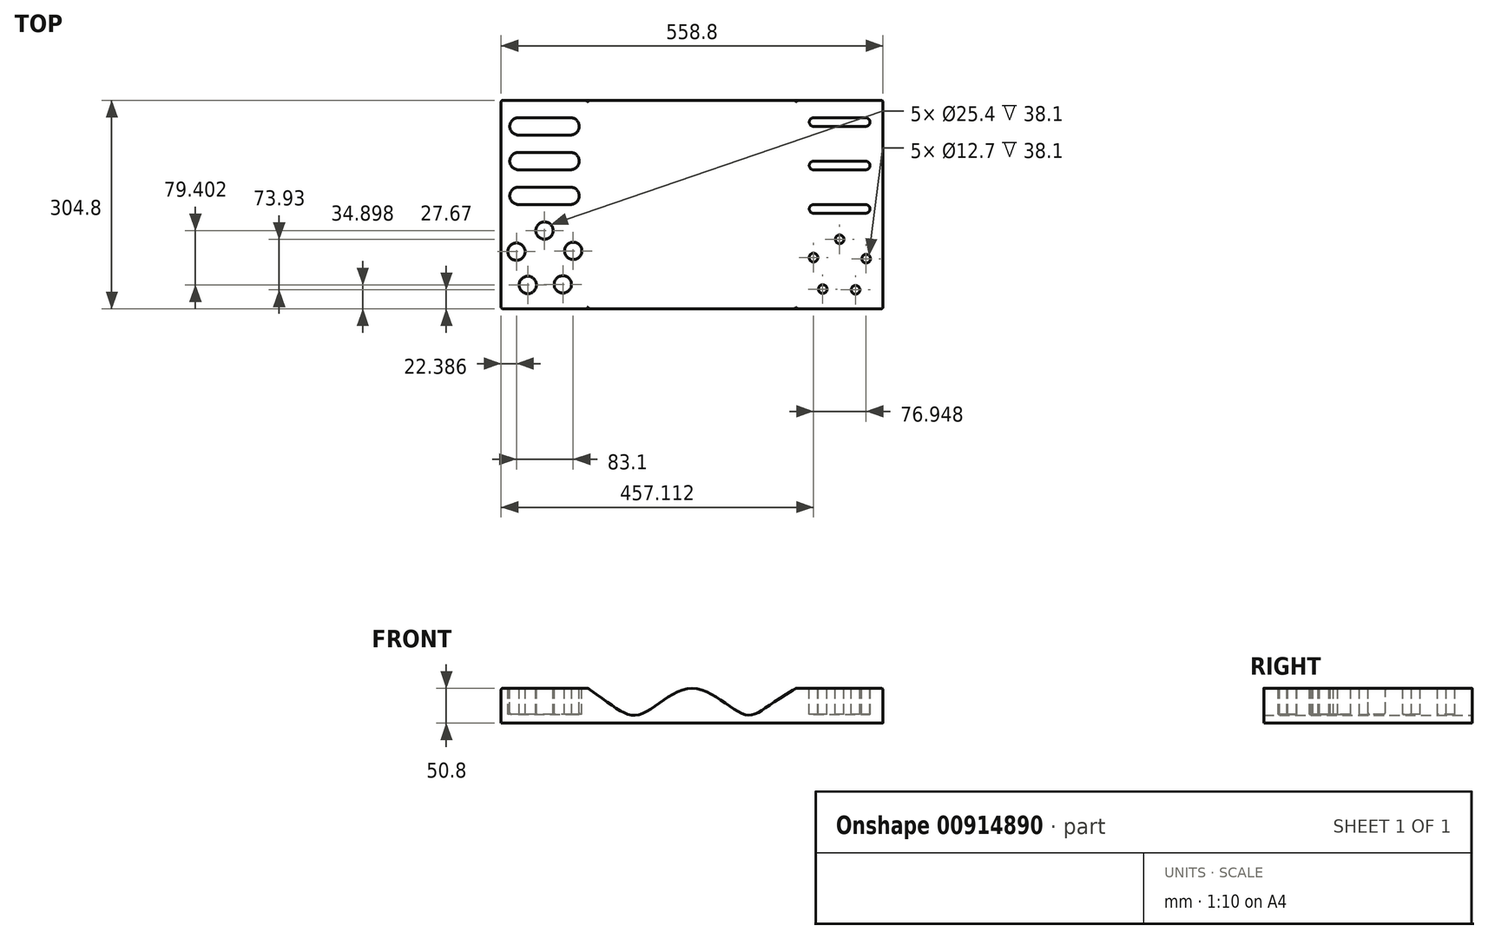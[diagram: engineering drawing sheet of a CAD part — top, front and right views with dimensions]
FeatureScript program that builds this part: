
annotation { "Feature Type Name" : "Feature", "Feature Type Description" : "" }
export const myFeature = defineFeature(function(context is Context, id is Id, definition is map)
    precondition{}
    {
        {
            var Q0;
            Q0=qCreatedBy(makeId("Front.planeOp"),FACE);
            var sketch = newSketch(context, id + "F0", { "sketchPlane" : qUnion([Q0])});
            skLineSegment(sketch, "E0.bottom", {"start": v(-259.7, 38.1) * mm, "end": v(-132.7, 38.1) * mm});
            skLineSegment(sketch, "E0.top", {"start": v(-259.7, -12.7) * mm, "end": v(299.1, -12.7) * mm});
            skLineSegment(sketch, "E0.left", {"start": v(-259.7, 38.1) * mm, "end": v(-259.7, -12.7) * mm});
            skLineSegment(sketch, "E0.right", {"start": v(299.1, 38.1) * mm, "end": v(299.1, -12.7) * mm});
            skPoint(sketch, "E1", {"position": v(172.1, 38.1) * mm});
            skPoint(sketch, "E2", {"position": v(19.7, 38.1) * mm});
            skPoint(sketch, "E3", {"position": v(-132.7, 38.1) * mm});
            skFitSpline(sketch, "E4", {"points": [v(172.1, 38.1) * mm, v(95.9, 0) * mm, v(19.7, 38.1) * mm, v(-56.5, 0) * mm, v(-132.7, 38.1) * mm], "startDerivative": vector(-541.44, -296.38) * mm, "endDerivative": vector(-454.84, 309.23) * mm});
            skLineSegment(sketch, "E5.trimOffspring", {"start": v(19.5, 38.1) * mm, "end": v(19.7, 38.1) * mm});
            skLineSegment(sketch, "E6.trimOffspring", {"start": v(172.1, 38.1) * mm, "end": v(299.1, 38.1) * mm});
            skSolve(sketch);
        }
        {
            var Q0;
            Q0=makeQuery(id+"F0.imprint","IMPRINT",FACE,{"disambiguationData":[TD([[makeQuery(id+"F0.imprint","IMPRINT",EDGE,{"derivedFrom":sQuery(id+"F0.wireOp",EDGE,"E0.bottom")}),-1.0]])]});
            extrude(context, id + "F1", {"entities" : qUnion([Q0]), "depth" : 304.8 * mm, "offsetDistance" : 25.4 * mm});
        }
        {
            var Q0;
            Q0=makeQuery(id+"F1.opExtrude","SWEPT_FACE",FACE,{"disambiguationData":[OSD([sQuery(id+"F0.wireOp",EDGE,"E0.bottom")])]});
            var sketch = newSketch(context, id + "F2", { "sketchPlane" : qUnion([Q0])});
            skLineSegment(sketch, "E7.bottom", {"start": v(-234.3, -25.4) * mm, "end": v(-158.1, -25.4) * mm});
            skLineSegment(sketch, "E7.top", {"start": v(-234.3, -50.8) * mm, "end": v(-158.1, -50.8) * mm});
            skArc(sketch, "E8", {"start": v(-234.3, -25.4) * mm, "mid": v(-247, -38.1) * mm, "end": v(-234.3, -50.8) * mm});
            skArc(sketch, "E9", {"start": v(-158.1, -50.8) * mm, "mid": v(-145.4, -38.1) * mm, "end": v(-158.1, -25.4) * mm});
            skArc(sketch, "E10.0.1.0", {"start": v(-234.3, -76.2) * mm, "mid": v(-247, -88.9) * mm, "end": v(-234.3, -101.6) * mm});
            skLineSegment(sketch, "E10.0.1.1", {"start": v(-234.3, -101.6) * mm, "end": v(-158.1, -101.6) * mm});
            skLineSegment(sketch, "E10.0.1.2", {"start": v(-234.3, -76.2) * mm, "end": v(-158.1, -76.2) * mm});
            skArc(sketch, "E10.0.1.3", {"start": v(-158.1, -101.6) * mm, "mid": v(-145.4, -88.9) * mm, "end": v(-158.1, -76.2) * mm});
            skArc(sketch, "E10.0.2.0", {"start": v(-234.3, -127) * mm, "mid": v(-247, -139.7) * mm, "end": v(-234.3, -152.4) * mm});
            skLineSegment(sketch, "E10.0.2.1", {"start": v(-234.3, -152.4) * mm, "end": v(-158.1, -152.4) * mm});
            skLineSegment(sketch, "E10.0.2.2", {"start": v(-234.3, -127) * mm, "end": v(-158.1, -127) * mm});
            skArc(sketch, "E10.0.2.3", {"start": v(-158.1, -152.4) * mm, "mid": v(-145.4, -139.7) * mm, "end": v(-158.1, -127) * mm});
            skLineSegment(sketch, "E10.direction1", {"start": v(-234.3, -50.8) * mm, "end": v(-208.9, -50.8) * mm, "construction": true});
            skLineSegment(sketch, "E10.direction2", {"start": v(-234.3, -50.8) * mm, "end": v(-234.3, -101.6) * mm, "construction": true});
            skCircle(sketch, "E11", {"center": v(-196.2, -190.5) * mm, "radius": 12.7 * mm});
            skCircle(sketch, "E12.1.0", {"center": v(-237.32, -221.29) * mm, "radius": 12.7 * mm});
            skCircle(sketch, "E12.2.0", {"center": v(-220.75, -269.9) * mm, "radius": 12.7 * mm});
            skCircle(sketch, "E12.3.0", {"center": v(-169.4, -269.16) * mm, "radius": 12.7 * mm});
            skCircle(sketch, "E12.4.0", {"center": v(-154.22, -220.09) * mm, "radius": 12.7 * mm});
            skPoint(sketch, "E12.center", {"position": v(-195.58, -234.19) * mm});
            skSolve(sketch);
        }
        {
            var Q0;
            Q0=makeQuery(id+"F2.imprint","IMPRINT",FACE,{"disambiguationData":[TD([[makeQuery(id+"F2.imprint","IMPRINT",EDGE,{"derivedFrom":sQuery(id+"F2.wireOp",EDGE,"E7.bottom")}),-1.0]])]});
            var Q1;
            Q1=makeQuery(id+"F2.imprint","IMPRINT",FACE,{"disambiguationData":[TD([[makeQuery(id+"F2.imprint","IMPRINT",EDGE,{"derivedFrom":sQuery(id+"F2.wireOp",EDGE,"E10.0.1.0")}),1.0]])]});
            var Q2;
            Q2=makeQuery(id+"F2.imprint","IMPRINT",FACE,{"disambiguationData":[TD([[makeQuery(id+"F2.imprint","IMPRINT",EDGE,{"derivedFrom":sQuery(id+"F2.wireOp",EDGE,"E10.0.2.0")}),1.0]])]});
            var Q3;
            Q3=makeQuery(id+"F2.imprint","IMPRINT",FACE,{"disambiguationData":[TD([[makeQuery(id+"F2.imprint","IMPRINT",EDGE,{"derivedFrom":sQuery(id+"F2.wireOp",EDGE,"E11")}),1.0]])]});
            var Q4;
            Q4=makeQuery(id+"F2.imprint","IMPRINT",FACE,{"disambiguationData":[TD([[makeQuery(id+"F2.imprint","IMPRINT",EDGE,{"derivedFrom":sQuery(id+"F2.wireOp",EDGE,"E12.4.0")}),1.0]])]});
            var Q5;
            Q5=makeQuery(id+"F2.imprint","IMPRINT",FACE,{"disambiguationData":[TD([[makeQuery(id+"F2.imprint","IMPRINT",EDGE,{"derivedFrom":sQuery(id+"F2.wireOp",EDGE,"E12.3.0")}),1.0]])]});
            var Q6;
            Q6=makeQuery(id+"F2.imprint","IMPRINT",FACE,{"disambiguationData":[TD([[makeQuery(id+"F2.imprint","IMPRINT",EDGE,{"derivedFrom":sQuery(id+"F2.wireOp",EDGE,"E12.2.0")}),1.0]])]});
            var Q7;
            Q7=makeQuery(id+"F2.imprint","IMPRINT",FACE,{"disambiguationData":[TD([[makeQuery(id+"F2.imprint","IMPRINT",EDGE,{"derivedFrom":sQuery(id+"F2.wireOp",EDGE,"E12.1.0")}),1.0]])]});
            extrude(context, id + "F3", {"entities" : qUnion([Q0, Q1, Q2, Q3, Q4, Q5, Q6, Q7]), "operationType" : NewBodyOperationType.REMOVE, "oppositeDirection" : true, "depth" : 38.1 * mm, "offsetDistance" : 25.4 * mm});
        }
        {
            var Q0;
            Q0=makeQuery(id+"F1.opExtrude","SWEPT_FACE",FACE,{"disambiguationData":[OSD([sQuery(id+"F0.wireOp",EDGE,"E6.trimOffspring")])]});
            var sketch = newSketch(context, id + "F4", { "sketchPlane" : qUnion([Q0])});
            skLineSegment(sketch, "E13.bottom", {"start": v(197.5, -25.4) * mm, "end": v(273.7, -25.4) * mm});
            skLineSegment(sketch, "E13.top", {"start": v(197.5, -38.1) * mm, "end": v(273.7, -38.1) * mm});
            skArc(sketch, "E14", {"start": v(273.7, -38.1) * mm, "mid": v(280.04, -31.75) * mm, "end": v(273.7, -25.4) * mm});
            skArc(sketch, "E15", {"start": v(197.5, -38.1) * mm, "mid": v(191.14, -31.75) * mm, "end": v(197.5, -25.4) * mm});
            skArc(sketch, "E16.0.1.0", {"start": v(273.7, -101.6) * mm, "mid": v(280.04, -95.25) * mm, "end": v(273.7, -88.9) * mm});
            skLineSegment(sketch, "E16.0.1.1", {"start": v(197.5, -101.6) * mm, "end": v(273.7, -101.6) * mm});
            skLineSegment(sketch, "E16.0.1.2", {"start": v(197.5, -88.9) * mm, "end": v(273.7, -88.9) * mm});
            skArc(sketch, "E16.0.1.3", {"start": v(197.5, -101.6) * mm, "mid": v(191.14, -95.25) * mm, "end": v(197.5, -88.9) * mm});
            skArc(sketch, "E16.0.2.0", {"start": v(273.7, -165.1) * mm, "mid": v(280.04, -158.75) * mm, "end": v(273.7, -152.4) * mm});
            skLineSegment(sketch, "E16.0.2.1", {"start": v(197.5, -165.1) * mm, "end": v(273.7, -165.1) * mm});
            skLineSegment(sketch, "E16.0.2.2", {"start": v(197.5, -152.4) * mm, "end": v(273.7, -152.4) * mm});
            skArc(sketch, "E16.0.2.3", {"start": v(197.5, -165.1) * mm, "mid": v(191.14, -158.75) * mm, "end": v(197.5, -152.4) * mm});
            skLineSegment(sketch, "E16.direction1", {"start": v(197.5, -38.1) * mm, "end": v(222.9, -38.1) * mm, "construction": true});
            skLineSegment(sketch, "E16.direction2", {"start": v(197.5, -38.1) * mm, "end": v(197.5, -101.6) * mm, "construction": true});
            skCircle(sketch, "E17", {"center": v(235.6, -203.2) * mm, "radius": 6.35 * mm});
            skCircle(sketch, "E18.1.0", {"center": v(274.35, -231.62) * mm, "radius": 6.35 * mm});
            skCircle(sketch, "E18.2.0", {"center": v(258.9, -277.13) * mm, "radius": 6.35 * mm});
            skCircle(sketch, "E18.3.0", {"center": v(210.85, -276.08) * mm, "radius": 6.35 * mm});
            skCircle(sketch, "E18.4.0", {"center": v(197.4, -229.94) * mm, "radius": 6.35 * mm});
            skPoint(sketch, "E18.center", {"position": v(235.6, -243.84) * mm});
            skLineSegment(sketch, "E18.anchor1", {"start": v(235.6, -243.84) * mm, "end": v(235.6, -203.2) * mm, "construction": true});
            skLineSegment(sketch, "E18.anchor2", {"start": v(235.6, -243.84) * mm, "end": v(197.4, -229.94) * mm, "construction": true});
            skSolve(sketch);
        }
        {
            var Q0;
            Q0=makeQuery(id+"F4.imprint","IMPRINT",FACE,{"disambiguationData":[TD([[makeQuery(id+"F4.imprint","IMPRINT",EDGE,{"derivedFrom":sQuery(id+"F4.wireOp",EDGE,"E13.bottom")}),-1.0]])]});
            var Q1;
            Q1=makeQuery(id+"F4.imprint","IMPRINT",FACE,{"disambiguationData":[TD([[makeQuery(id+"F4.imprint","IMPRINT",EDGE,{"derivedFrom":sQuery(id+"F4.wireOp",EDGE,"E16.0.1.0")}),1.0]])]});
            var Q2;
            Q2=makeQuery(id+"F4.imprint","IMPRINT",FACE,{"disambiguationData":[TD([[makeQuery(id+"F4.imprint","IMPRINT",EDGE,{"derivedFrom":sQuery(id+"F4.wireOp",EDGE,"E16.0.2.0")}),1.0]])]});
            var Q3;
            Q3=makeQuery(id+"F4.imprint","IMPRINT",FACE,{"disambiguationData":[TD([[makeQuery(id+"F4.imprint","IMPRINT",EDGE,{"derivedFrom":sQuery(id+"F4.wireOp",EDGE,"E17")}),1.0]])]});
            var Q4;
            Q4=makeQuery(id+"F4.imprint","IMPRINT",FACE,{"disambiguationData":[TD([[makeQuery(id+"F4.imprint","IMPRINT",EDGE,{"derivedFrom":sQuery(id+"F4.wireOp",EDGE,"E18.1.0")}),1.0]])]});
            var Q5;
            Q5=makeQuery(id+"F4.imprint","IMPRINT",FACE,{"disambiguationData":[TD([[makeQuery(id+"F4.imprint","IMPRINT",EDGE,{"derivedFrom":sQuery(id+"F4.wireOp",EDGE,"E18.2.0")}),1.0]])]});
            var Q6;
            Q6=makeQuery(id+"F4.imprint","IMPRINT",FACE,{"disambiguationData":[TD([[makeQuery(id+"F4.imprint","IMPRINT",EDGE,{"derivedFrom":sQuery(id+"F4.wireOp",EDGE,"E18.3.0")}),1.0]])]});
            var Q7;
            Q7=makeQuery(id+"F4.imprint","IMPRINT",FACE,{"disambiguationData":[TD([[makeQuery(id+"F4.imprint","IMPRINT",EDGE,{"derivedFrom":sQuery(id+"F4.wireOp",EDGE,"E18.4.0")}),1.0]])]});
            extrude(context, id + "F5", {"entities" : qUnion([Q0, Q1, Q2, Q3, Q4, Q5, Q6, Q7]), "operationType" : NewBodyOperationType.REMOVE, "oppositeDirection" : true, "depth" : 38.1 * mm, "offsetDistance" : 25.4 * mm});
        }
        {
            var Q0;
            Q0=makeQuery(id+"F1.opExtrude","SWEPT_EDGE",EDGE,{"disambiguationData":[OSD([sQuery(id+"F0.wireOp",EDGE,"E0.bottom"),sQuery(id+"F0.wireOp",EDGE,"E4")])]});
            var Q1;
            Q1=makeQuery(id+"F1.opExtrude","CAP_EDGE",EDGE,{"disambiguationData":[OSD([sQuery(id+"F0.wireOp",EDGE,"E0.bottom")])],"isStart":false});
            var Q2;
            Q2=makeQuery(id+"F1.opExtrude","SWEPT_EDGE",EDGE,{"disambiguationData":[OSD([sQuery(id+"F0.wireOp",EDGE,"E0.bottom"),sQuery(id+"F0.wireOp",EDGE,"E0.left")])]});
            var Q3;
            Q3=makeQuery(id+"F1.opExtrude","CAP_EDGE",EDGE,{"disambiguationData":[OSD([sQuery(id+"F0.wireOp",EDGE,"E0.bottom")])],"isStart":true});
            var Q4;
            Q4=makeQuery(id+"F3.boolean.opBoolean","COPY",EDGE,{"derivedFrom":makeQuery(id+"F3.opExtrude","CAP_EDGE",EDGE,{"disambiguationData":[OSD([sQuery(id+"F2.wireOp",EDGE,"E7.bottom")])],"isStart":true})});
            var Q5;
            Q5=makeQuery(id+"F3.boolean.opBoolean","COPY",EDGE,{"derivedFrom":makeQuery(id+"F3.opExtrude","CAP_EDGE",EDGE,{"disambiguationData":[OSD([sQuery(id+"F2.wireOp",EDGE,"E8")])],"isStart":true})});
            var Q6;
            Q6=makeQuery(id+"F3.boolean.opBoolean","COPY",EDGE,{"derivedFrom":makeQuery(id+"F3.opExtrude","CAP_EDGE",EDGE,{"disambiguationData":[OSD([sQuery(id+"F2.wireOp",EDGE,"E10.0.1.3")])],"isStart":true})});
            var Q7;
            Q7=makeQuery(id+"F3.boolean.opBoolean","COPY",FACE,{"derivedFrom":makeQuery(id+"F3.opExtrude","SWEPT_FACE",FACE,{"disambiguationData":[OSD([sQuery(id+"F2.wireOp",EDGE,"E10.0.2.3")])]})});
            var Q8;
            Q8=makeQuery(id+"F3.boolean.opBoolean","COPY",EDGE,{"derivedFrom":makeQuery(id+"F3.opExtrude","CAP_EDGE",EDGE,{"disambiguationData":[OSD([sQuery(id+"F2.wireOp",EDGE,"E11")])],"isStart":true})});
            var Q9;
            Q9=makeQuery(id+"F3.boolean.opBoolean","COPY",EDGE,{"derivedFrom":makeQuery(id+"F3.opExtrude","CAP_EDGE",EDGE,{"disambiguationData":[OSD([sQuery(id+"F2.wireOp",EDGE,"E12.4.0")])],"isStart":true})});
            var Q10;
            Q10=makeQuery(id+"F3.boolean.opBoolean","COPY",EDGE,{"derivedFrom":makeQuery(id+"F3.opExtrude","CAP_EDGE",EDGE,{"disambiguationData":[OSD([sQuery(id+"F2.wireOp",EDGE,"E12.3.0")])],"isStart":true})});
            var Q11;
            Q11=makeQuery(id+"F3.boolean.opBoolean","COPY",EDGE,{"derivedFrom":makeQuery(id+"F3.opExtrude","CAP_EDGE",EDGE,{"disambiguationData":[OSD([sQuery(id+"F2.wireOp",EDGE,"E12.2.0")])],"isStart":true})});
            var Q12;
            Q12=makeQuery(id+"F3.boolean.opBoolean","COPY",EDGE,{"derivedFrom":makeQuery(id+"F3.opExtrude","CAP_EDGE",EDGE,{"disambiguationData":[OSD([sQuery(id+"F2.wireOp",EDGE,"E12.1.0")])],"isStart":true})});
            var Q13;
            Q13=makeQuery(id+"F1.opExtrude","SWEPT_EDGE",EDGE,{"disambiguationData":[OSD([sQuery(id+"F0.wireOp",EDGE,"E4"),sQuery(id+"F0.wireOp",EDGE,"E6.trimOffspring")])]});
            var Q14;
            Q14=makeQuery(id+"F1.opExtrude","CAP_EDGE",EDGE,{"disambiguationData":[OSD([sQuery(id+"F0.wireOp",EDGE,"E6.trimOffspring")])],"isStart":false});
            var Q15;
            Q15=makeQuery(id+"F1.opExtrude","SWEPT_EDGE",EDGE,{"disambiguationData":[OSD([sQuery(id+"F0.wireOp",EDGE,"E0.right"),sQuery(id+"F0.wireOp",EDGE,"E6.trimOffspring")])]});
            var Q16;
            Q16=makeQuery(id+"F1.opExtrude","CAP_EDGE",EDGE,{"disambiguationData":[OSD([sQuery(id+"F0.wireOp",EDGE,"E6.trimOffspring")])],"isStart":true});
            var Q17;
            Q17=makeQuery(id+"F5.boolean.opBoolean","COPY",EDGE,{"derivedFrom":makeQuery(id+"F5.opExtrude","CAP_EDGE",EDGE,{"disambiguationData":[OSD([sQuery(id+"F4.wireOp",EDGE,"E14")])],"isStart":true})});
            var Q18;
            Q18=makeQuery(id+"F5.boolean.opBoolean","COPY",EDGE,{"derivedFrom":makeQuery(id+"F5.opExtrude","CAP_EDGE",EDGE,{"disambiguationData":[OSD([sQuery(id+"F4.wireOp",EDGE,"E16.0.1.0")])],"isStart":true})});
            var Q19;
            Q19=makeQuery(id+"F5.boolean.opBoolean","COPY",EDGE,{"derivedFrom":makeQuery(id+"F5.opExtrude","CAP_EDGE",EDGE,{"disambiguationData":[OSD([sQuery(id+"F4.wireOp",EDGE,"E16.0.2.0")])],"isStart":true})});
            var Q20;
            Q20=makeQuery(id+"F5.boolean.opBoolean","COPY",EDGE,{"derivedFrom":makeQuery(id+"F5.opExtrude","CAP_EDGE",EDGE,{"disambiguationData":[OSD([sQuery(id+"F4.wireOp",EDGE,"E18.1.0")])],"isStart":true})});
            var Q21;
            Q21=makeQuery(id+"F5.boolean.opBoolean","COPY",EDGE,{"derivedFrom":makeQuery(id+"F5.opExtrude","CAP_EDGE",EDGE,{"disambiguationData":[OSD([sQuery(id+"F4.wireOp",EDGE,"E17")])],"isStart":true})});
            var Q22;
            Q22=makeQuery(id+"F5.boolean.opBoolean","COPY",EDGE,{"derivedFrom":makeQuery(id+"F5.opExtrude","CAP_EDGE",EDGE,{"disambiguationData":[OSD([sQuery(id+"F4.wireOp",EDGE,"E18.4.0")])],"isStart":true})});
            var Q23;
            Q23=makeQuery(id+"F5.boolean.opBoolean","COPY",EDGE,{"derivedFrom":makeQuery(id+"F5.opExtrude","CAP_EDGE",EDGE,{"disambiguationData":[OSD([sQuery(id+"F4.wireOp",EDGE,"E18.3.0")])],"isStart":true})});
            var Q24;
            Q24=makeQuery(id+"F5.boolean.opBoolean","COPY",EDGE,{"derivedFrom":makeQuery(id+"F5.opExtrude","CAP_EDGE",EDGE,{"disambiguationData":[OSD([sQuery(id+"F4.wireOp",EDGE,"E18.2.0")])],"isStart":true})});
            var Q25;
            Q25=makeQuery(id+"F1.opExtrude","CAP_EDGE",EDGE,{"disambiguationData":[OSD([sQuery(id+"F0.wireOp",EDGE,"E0.right")])],"isStart":false});
            var Q26;
            Q26=makeQuery(id+"F1.opExtrude","CAP_EDGE",EDGE,{"disambiguationData":[OSD([sQuery(id+"F0.wireOp",EDGE,"E0.right")])],"isStart":true});
            var Q27;
            Q27=makeQuery(id+"F1.opExtrude","CAP_EDGE",EDGE,{"disambiguationData":[OSD([sQuery(id+"F0.wireOp",EDGE,"E0.left")])],"isStart":true});
            var Q28;
            Q28=makeQuery(id+"F1.opExtrude","CAP_EDGE",EDGE,{"disambiguationData":[OSD([sQuery(id+"F0.wireOp",EDGE,"E0.left")])],"isStart":false});
            var Q29;
            Q29=makeQuery(id+"F5.boolean.opBoolean","COPY",EDGE,{"derivedFrom":makeQuery(id+"F5.opExtrude","CAP_EDGE",EDGE,{"disambiguationData":[OSD([sQuery(id+"F4.wireOp",EDGE,"E16.0.1.2")])],"isStart":true})});
            var Q30;
            Q30=makeQuery(id+"F5.boolean.opBoolean","COPY",EDGE,{"derivedFrom":makeQuery(id+"F5.opExtrude","CAP_EDGE",EDGE,{"disambiguationData":[OSD([sQuery(id+"F4.wireOp",EDGE,"E16.0.1.1")])],"isStart":true})});
            var Q31;
            Q31=makeQuery(id+"F5.boolean.opBoolean","COPY",EDGE,{"derivedFrom":makeQuery(id+"F5.opExtrude","CAP_EDGE",EDGE,{"disambiguationData":[OSD([sQuery(id+"F4.wireOp",EDGE,"E16.0.1.3")])],"isStart":true})});
            var Q32;
            Q32=makeQuery(id+"F5.boolean.opBoolean","COPY",EDGE,{"derivedFrom":makeQuery(id+"F5.opExtrude","CAP_EDGE",EDGE,{"disambiguationData":[OSD([sQuery(id+"F4.wireOp",EDGE,"E16.0.2.3")])],"isStart":true})});
            var Q33;
            Q33=makeQuery(id+"F5.boolean.opBoolean","COPY",EDGE,{"derivedFrom":makeQuery(id+"F5.opExtrude","CAP_EDGE",EDGE,{"disambiguationData":[OSD([sQuery(id+"F4.wireOp",EDGE,"E16.0.2.2")])],"isStart":true})});
            var Q34;
            Q34=makeQuery(id+"F5.boolean.opBoolean","COPY",EDGE,{"derivedFrom":makeQuery(id+"F5.opExtrude","CAP_EDGE",EDGE,{"disambiguationData":[OSD([sQuery(id+"F4.wireOp",EDGE,"E16.0.2.1")])],"isStart":true})});
            var Q35;
            Q35=makeQuery(id+"F5.boolean.opBoolean","COPY",EDGE,{"derivedFrom":makeQuery(id+"F5.opExtrude","CAP_EDGE",EDGE,{"disambiguationData":[OSD([sQuery(id+"F4.wireOp",EDGE,"E13.top")])],"isStart":true})});
            var Q36;
            Q36=makeQuery(id+"F5.boolean.opBoolean","COPY",EDGE,{"derivedFrom":makeQuery(id+"F5.opExtrude","CAP_EDGE",EDGE,{"disambiguationData":[OSD([sQuery(id+"F4.wireOp",EDGE,"E13.bottom")])],"isStart":true})});
            var Q37;
            Q37=makeQuery(id+"F5.boolean.opBoolean","COPY",EDGE,{"derivedFrom":makeQuery(id+"F5.opExtrude","CAP_EDGE",EDGE,{"disambiguationData":[OSD([sQuery(id+"F4.wireOp",EDGE,"E15")])],"isStart":true})});
            fillet(context, id + "F6", {"entities" : qUnion([Q0, Q1, Q2, Q3, Q4, Q5, Q6, Q7, Q8, Q9, Q10, Q11, Q12, Q13, Q14, Q15, Q16, Q17, Q18, Q19, Q20, Q21, Q22, Q23, Q24, Q25, Q26, Q27, Q28, Q29, Q30, Q31, Q32, Q33, Q34, Q35, Q36, Q37]), "radius" : 2.54 * mm, "tangentPropagation" : true, "allowEdgeOverflow" : false});
        }
    });
